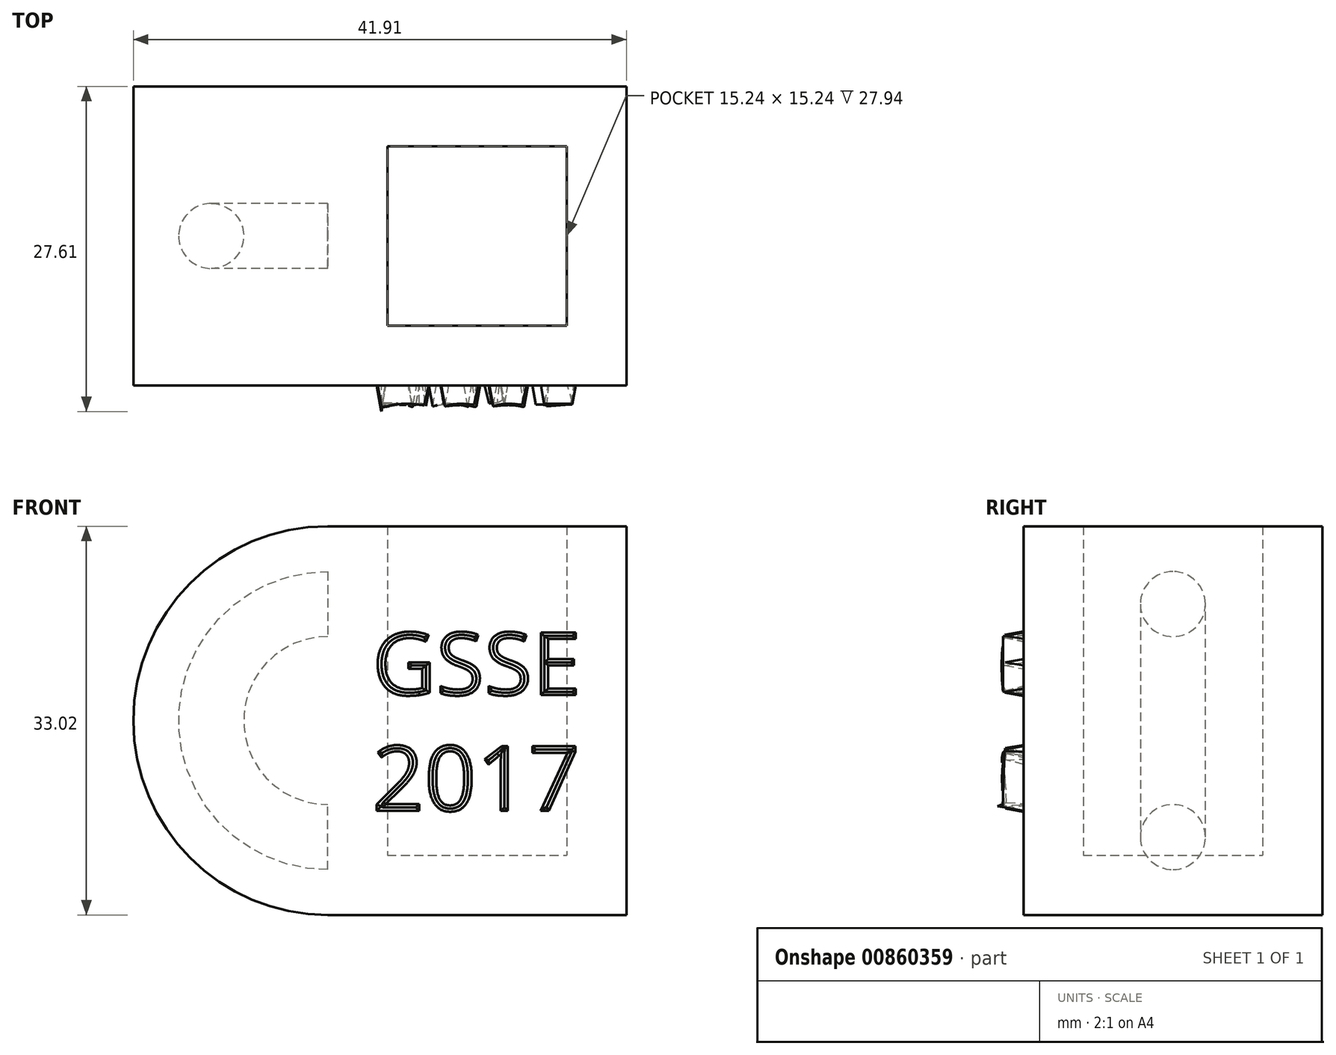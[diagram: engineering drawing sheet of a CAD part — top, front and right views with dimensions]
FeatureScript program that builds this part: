
annotation { "Feature Type Name" : "Feature", "Feature Type Description" : "" }
export const myFeature = defineFeature(function(context is Context, id is Id, definition is map)
    precondition{}
    {
        {
            var Q0;
            Q0=qCreatedBy(makeId("Front.planeOp"),FACE);
            var sketch = newSketch(context, id + "F0", { "sketchPlane" : qUnion([Q0])});
            skLineSegment(sketch, "E0.bottom", {"start": v(-12.7, 16.51) * mm, "end": v(12.7, 16.51) * mm});
            skLineSegment(sketch, "E0.top", {"start": v(-12.7, -16.51) * mm, "end": v(12.7, -16.51) * mm});
            skLineSegment(sketch, "E0.left", {"start": v(-12.7, 16.51) * mm, "end": v(-12.7, -16.51) * mm});
            skLineSegment(sketch, "E0.right", {"start": v(12.7, 16.51) * mm, "end": v(12.7, -16.51) * mm});
            skLineSegment(sketch, "E1", {"start": v(0, 0) * mm, "end": v(12.7, 0) * mm, "construction": true});
            skLineSegment(sketch, "E2", {"start": v(0, 0) * mm, "end": v(0, -16.51) * mm, "construction": true});
            skLineSegment(sketch, "E3", {"start": v(0, 0) * mm, "end": v(0, 16.51) * mm, "construction": true});
            skLineSegment(sketch, "E4", {"start": v(0, 0) * mm, "end": v(-12.7, 0) * mm, "construction": true});
            skSolve(sketch);
        }
        {
            var Q0;
            Q0=makeQuery(id+"F0.imprint","IMPRINT",FACE,{"disambiguationData":[TD([[makeQuery(id+"F0.imprint","IMPRINT",EDGE,{"derivedFrom":sQuery(id+"F0.wireOp",EDGE,"E0.bottom")}),-1.0]])]});
            extrude(context, id + "F1", {"entities" : qUnion([Q0]), "depth" : 25.4 * mm, "offsetDistance" : 25.4 * mm});
        }
        {
            var Q0;
            Q0=makeQuery(id+"F1.opExtrude","SWEPT_FACE",FACE,{"disambiguationData":[OSD([sQuery(id+"F0.wireOp",EDGE,"E0.bottom")])]});
            var Q1;
            Q1=makeQuery(id+"F1.opExtrude","SWEPT_BODY",BODY,{"disambiguationData":[OSD([sQuery(id+"F0.wireOp",EDGE,"E0.bottom"),sQuery(id+"F0.wireOp",EDGE,"E0.top"),sQuery(id+"F0.wireOp",EDGE,"E0.left"),sQuery(id+"F0.wireOp",EDGE,"E0.right")])]});
            shell(context, id + "F2", {"entities" : qUnion([Q0]), "parts" : qUnion([Q1]), "thickness" : 5.08 * mm});
        }
        {
            var Q0;
            Q0=makeQuery(id+"F1.opExtrude","CAP_FACE",FACE,{"disambiguationData":[OSD([sQuery(id+"F0.wireOp",EDGE,"E0.bottom"),sQuery(id+"F0.wireOp",EDGE,"E0.top"),sQuery(id+"F0.wireOp",EDGE,"E0.left"),sQuery(id+"F0.wireOp",EDGE,"E0.right")])],"isStart":false});
            var sketch = newSketch(context, id + "F3", { "sketchPlane" : qUnion([Q0])});
            skText(sketch, "E5", { "text": "GSSE", "fontName": "OpenSans-Regular.ttf"});
            skText(sketch, "E6", { "text": "2017", "fontName": "OpenSans-Regular.ttf"});
            skLineSegment(sketch, "E7", {"start": v(0, 0) * mm, "end": v(8.9, 0) * mm, "construction": true});
            skLineSegment(sketch, "E8", {"start": v(0, 0) * mm, "end": v(-8.89, 0) * mm, "construction": true});
            const initialGuessF3  = {"E5": [-0.0089, 0.00217, 1, 0, 0.00536], "E6": [-0.0089, -0.00767, 1, 0, 0.00556]};
            skSetInitialGuess(sketch, initialGuessF3);
            skSolve(sketch);
        }
        {
            var Q0;
            Q0 = qSketchRegion(id + "F3", true);
            extrude(context, id + "F4", {"entities" : qUnion([Q0]), "operationType" : NewBodyOperationType.ADD, "depth" : 2.54 * mm, "offsetDistance" : 25.4 * mm, "hasDraft" : true, "draftAngle" : 10 * degree, "draftPullDirection" : true});
        }
        {
            var Q0;
            Q0=makeQuery(id+"F1.opExtrude","SWEPT_FACE",FACE,{"disambiguationData":[OSD([sQuery(id+"F0.wireOp",EDGE,"E0.left")])]});
            var sketch = newSketch(context, id + "F5", { "sketchPlane" : qUnion([Q0])});
            skLineSegment(sketch, "E9", {"start": v(0, 9.9) * mm, "end": v(25.4, 9.9) * mm});
            skCircle(sketch, "E10", {"center": v(12.7, 9.9) * mm, "radius": 2.76 * mm});
            skLineSegment(sketch, "E11", {"start": v(0, 0) * mm, "end": v(25.4, 0) * mm});
            skSolve(sketch);
        }
        {
            var Q0;
            {var subQ0=sQuery(id+"F5.wireOp",EDGE,"E10");var subQ1=sQuery(id+"F5.wireOp",EDGE,"E9");var subQ2=makeQuery(id+"F5.imprint","INTERSECT",VERTEX,{"disambiguationData":[OD(0.0)],"derivedFrom":[subQ1,subQ0]});Q0=makeQuery(id+"F5.imprint","IMPRINT",FACE,{"disambiguationData":[TD([[makeQuery(id+"F5.imprint","IMPRINT",EDGE,{"disambiguationData":[TD([[subQ2,-1.0]])],"derivedFrom":subQ1}),1.0]])]});}
            var Q1;
            {var subQ0=sQuery(id+"F5.wireOp",EDGE,"E10");var subQ1=sQuery(id+"F5.wireOp",EDGE,"E9");var subQ2=makeQuery(id+"F5.imprint","INTERSECT",VERTEX,{"disambiguationData":[OD(0.0)],"derivedFrom":[subQ1,subQ0]});Q1=makeQuery(id+"F5.imprint","IMPRINT",FACE,{"disambiguationData":[TD([[makeQuery(id+"F5.imprint","IMPRINT",EDGE,{"disambiguationData":[TD([[subQ2,-1.0]])],"derivedFrom":subQ1}),-1.0]])]});}
            var Q2;
            Q2=sQuery(id+"F5.wireOp",EDGE,"E11");
            revolve(context, id + "F6", {"operationType" : NewBodyOperationType.ADD, "surfaceOperationType" : NewSurfaceOperationType.NEW, "entities" : qUnion([Q0, Q1]), "axis" : qUnion([Q2]), "revolveType" : RevolveType.ONE_DIRECTION, "angle" : 185 * degree});
        }
    });
